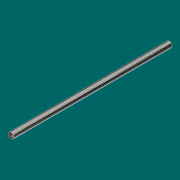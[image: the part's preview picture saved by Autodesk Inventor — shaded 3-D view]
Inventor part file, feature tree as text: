
AUTODESK INVENTOR PART (.ipt)
format: ipt  version: 2017 (Build 210142000, 142)  size: 69,120 bytes
history: native  units: in
note: dims shown in document units (in); Inventor stores cm internally (conversion verified against a paired STEP export)
features: extrude x1, sketch x1
ambient origin geometry x8: Origin, YZ Plane, XZ Plane, XY Plane, X Axis, Y Axis, Z Axis, Center Point
bodies: Solid1 (feature_tree)
feature tree (2):
  extrude  "Extrusion1"  Depth=60.0in TaperAngle=0.0deg
  sketch  "Sketch1"  dims[d0=2.25in d1=60.0in d2=0.0in]
